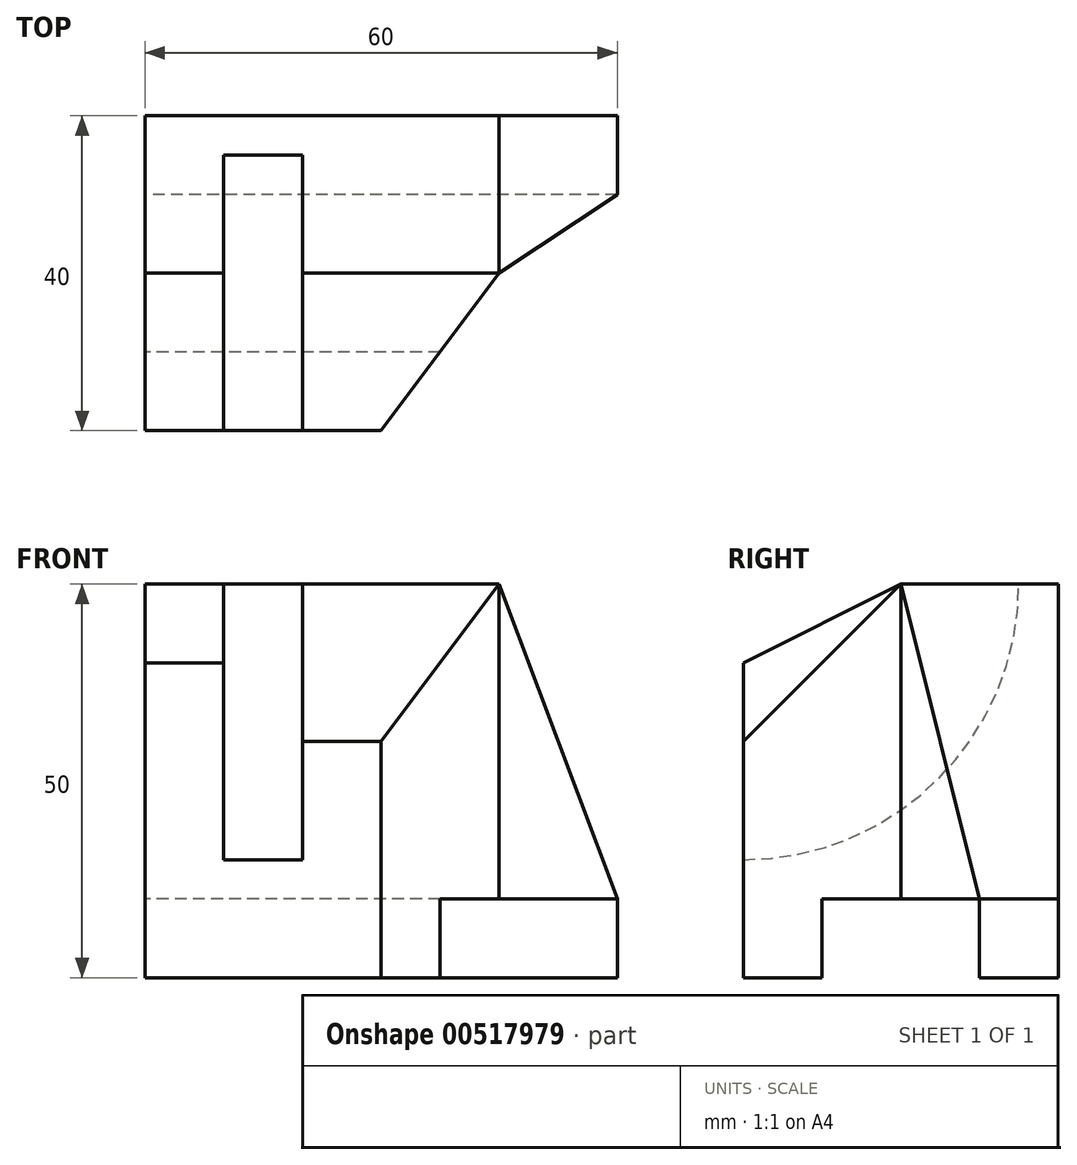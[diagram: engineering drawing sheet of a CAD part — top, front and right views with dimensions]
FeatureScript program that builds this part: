
annotation { "Feature Type Name" : "Feature", "Feature Type Description" : "" }
export const myFeature = defineFeature(function(context is Context, id is Id, definition is map)
    precondition{}
    {
        {
            var Q0;
            Q0=qCreatedBy(makeId("Top.planeOp"),FACE);
            var sketch = newSketch(context, id + "F0", { "sketchPlane" : qUnion([Q0])});
            skLineSegment(sketch, "E0.bottom", {"start": v(0, 0) * mm, "end": v(60, 0) * mm});
            skLineSegment(sketch, "E0.top", {"start": v(0, 40) * mm, "end": v(60, 40) * mm});
            skLineSegment(sketch, "E0.left", {"start": v(0, 0) * mm, "end": v(0, 40) * mm});
            skLineSegment(sketch, "E0.right", {"start": v(60, 0) * mm, "end": v(60, 40) * mm});
            skSolve(sketch);
        }
        {
            var Q0;
            Q0 = qSketchRegion(id + "F0", true);
            extrude(context, id + "F1", {"entities" : qUnion([Q0]), "depth" : 50 * mm, "offsetDistance" : 25 * mm});
        }
        {
            var Q0;
            Q0=makeQuery(id+"F1.opExtrude","CAP_FACE",FACE,{"disambiguationData":[OSD([sQuery(id+"F0.wireOp",EDGE,"E0.bottom"),sQuery(id+"F0.wireOp",EDGE,"E0.top"),sQuery(id+"F0.wireOp",EDGE,"E0.left"),sQuery(id+"F0.wireOp",EDGE,"E0.right")])],"isStart":true});
            var sketch = newSketch(context, id + "F2", { "sketchPlane" : qUnion([Q0])});
            skLineSegment(sketch, "E1.bottom", {"start": v(60, -10) * mm, "end": v(0, -10) * mm});
            skLineSegment(sketch, "E1.top", {"start": v(60, -30) * mm, "end": v(0, -30) * mm});
            skLineSegment(sketch, "E1.left", {"start": v(60, -10) * mm, "end": v(60, -30) * mm});
            skLineSegment(sketch, "E1.right", {"start": v(0, -10) * mm, "end": v(0, -30) * mm});
            skSolve(sketch);
        }
        {
            var Q0;
            Q0=makeQuery(id+"F2.imprint","IMPRINT",FACE,{"disambiguationData":[TD([[makeQuery(id+"F2.imprint","IMPRINT",EDGE,{"derivedFrom":sQuery(id+"F2.wireOp",EDGE,"E1.bottom")}),1.0]])]});
            extrude(context, id + "F3", {"entities" : qUnion([Q0]), "operationType" : NewBodyOperationType.REMOVE, "oppositeDirection" : true, "depth" : 10 * mm, "offsetDistance" : 25 * mm});
        }
        {
            var Q0;
            Q0=makeQuery(id+"F1.opExtrude","CAP_FACE",FACE,{"disambiguationData":[OSD([sQuery(id+"F0.wireOp",EDGE,"E0.bottom"),sQuery(id+"F0.wireOp",EDGE,"E0.top"),sQuery(id+"F0.wireOp",EDGE,"E0.left"),sQuery(id+"F0.wireOp",EDGE,"E0.right")])],"isStart":false});
            var sketch = newSketch(context, id + "F4", { "sketchPlane" : qUnion([Q0])});
            skLineSegment(sketch, "E2.bottom", {"start": v(10, 0) * mm, "end": v(20, 0) * mm});
            skLineSegment(sketch, "E2.top", {"start": v(10, 35) * mm, "end": v(20, 35) * mm});
            skLineSegment(sketch, "E2.left", {"start": v(10, 0) * mm, "end": v(10, 35) * mm});
            skLineSegment(sketch, "E2.right", {"start": v(20, 0) * mm, "end": v(20, 35) * mm});
            skSolve(sketch);
        }
        {
            var Q0;
            Q0=makeQuery(id+"F4.imprint","IMPRINT",FACE,{"disambiguationData":[TD([[makeQuery(id+"F4.imprint","IMPRINT",EDGE,{"derivedFrom":sQuery(id+"F4.wireOp",EDGE,"E2.bottom")}),1.0]])]});
            extrude(context, id + "F5", {"entities" : qUnion([Q0]), "operationType" : NewBodyOperationType.REMOVE, "oppositeDirection" : true, "depth" : 35 * mm, "offsetDistance" : 25 * mm});
        }
        {
            var Q0;
            Q0=makeQuery(id+"F5.boolean.opBoolean","COPY",EDGE,{"derivedFrom":makeQuery(id+"F5.opExtrude","CAP_EDGE",EDGE,{"disambiguationData":[OSD([sQuery(id+"F4.wireOp",EDGE,"E2.top")])],"isStart":false})});
            fillet(context, id + "F6", {"entities" : qUnion([Q0]), "radius" : 35 * mm, "tangentPropagation" : true, "allowEdgeOverflow" : false});
        }
        {
            var Q0;
            Q0=makeQuery(id+"F1.opExtrude","SWEPT_FACE",FACE,{"disambiguationData":[OSD([sQuery(id+"F0.wireOp",EDGE,"E0.left")])]});
            var sketch = newSketch(context, id + "F7", { "sketchPlane" : qUnion([Q0])});
            skLineSegment(sketch, "E3", {"start": v(-20, 50) * mm, "end": v(0, 40) * mm});
            skSolve(sketch);
        }
        {
            var Q0;
            {var subQ0=sQuery(id+"F7.wireOp",EDGE,"E3");Q0=makeQuery(id+"F7.imprint","IMPRINT",FACE,{"disambiguationData":[TD([[makeQuery(id+"F7.imprint","IMPRINT",EDGE,{"derivedFrom":subQ0}),1.0]])]});}
            extrude(context, id + "F8", {"entities" : qUnion([Q0]), "operationType" : NewBodyOperationType.REMOVE, "endBound" : BoundingType.UP_TO_NEXT, "oppositeDirection" : true, "depth" : 25 * mm, "offsetDistance" : 25 * mm});
        }
        {
            var Q0;
            Q0=makeQuery(id+"F1.opExtrude","CAP_FACE",FACE,{"disambiguationData":[OSD([sQuery(id+"F0.wireOp",EDGE,"E0.bottom"),sQuery(id+"F0.wireOp",EDGE,"E0.top"),sQuery(id+"F0.wireOp",EDGE,"E0.left"),sQuery(id+"F0.wireOp",EDGE,"E0.right")])],"isStart":false});
            var sketch = newSketch(context, id + "F9", { "sketchPlane" : qUnion([Q0])});
            skLineSegment(sketch, "E4", {"start": v(30, 0) * mm, "end": v(45, 20) * mm});
            skLineSegment(sketch, "E5", {"start": v(45, 20) * mm, "end": v(60, 20) * mm});
            skPoint(sketch, "E5.endSnap0", {"position": v(60, 20) * mm});
            skSolve(sketch);
        }
        {
            var Q0;
            {var subQ0=sQuery(id+"F9.wireOp",EDGE,"E4");Q0=makeQuery(id+"F9.imprint","IMPRINT",FACE,{"disambiguationData":[TD([[makeQuery(id+"F9.imprint","IMPRINT",EDGE,{"derivedFrom":subQ0}),-1.0]])]});}
            extrude(context, id + "F10", {"entities" : qUnion([Q0]), "operationType" : NewBodyOperationType.REMOVE, "endBound" : BoundingType.THROUGH_ALL, "oppositeDirection" : true, "depth" : 25 * mm, "offsetDistance" : 25 * mm});
        }
        {
            var Q0;
            Q0=makeQuery(id+"F1.opExtrude","CAP_FACE",FACE,{"disambiguationData":[OSD([sQuery(id+"F0.wireOp",EDGE,"E0.bottom"),sQuery(id+"F0.wireOp",EDGE,"E0.top"),sQuery(id+"F0.wireOp",EDGE,"E0.left"),sQuery(id+"F0.wireOp",EDGE,"E0.right")])],"isStart":false});
            var sketch = newSketch(context, id + "F11", { "sketchPlane" : qUnion([Q0])});
            skLineSegment(sketch, "E6", {"start": v(20, 20) * mm, "end": v(45, 20) * mm});
            skPoint(sketch, "E6.startSnap0", {"position": v(5, 20) * mm});
            skSolve(sketch);
        }
        {
            var Q0;
            Q0=makeQuery(id+"F10.boolean.opBoolean","COPY",FACE,{"derivedFrom":makeQuery(id+"F10.opExtrude","SWEPT_FACE",FACE,{"disambiguationData":[OSD([sQuery(id+"F9.wireOp",EDGE,"E4")])]})});
            var sketch = newSketch(context, id + "F12", { "sketchPlane" : qUnion([Q0])});
            skLineSegment(sketch, "E7", {"start": v(43, 50) * mm, "end": v(18, 30) * mm});
            skSolve(sketch);
        }
        {
            var Q0;
            {var subQ0=sQuery(id+"F11.wireOp",EDGE,"E6");Q0=makeQuery(id+"F11.imprint","IMPRINT",FACE,{"disambiguationData":[TD([[makeQuery(id+"F11.imprint","IMPRINT",EDGE,{"derivedFrom":subQ0}),-1.0]])]});}
            var Q1;
            Q1=sQuery(id+"F12.wireOp",EDGE,"E7");
            sweep(context, id + "F13", {"operationType" : NewBodyOperationType.REMOVE, "profiles" : qUnion([Q0]), "path" : qUnion([Q1])});
        }
        {
            var Q0;
            Q0=makeQuery(id+"F1.opExtrude","SWEPT_FACE",FACE,{"disambiguationData":[OSD([sQuery(id+"F0.wireOp",EDGE,"E0.bottom")])]});
            var sketch = newSketch(context, id + "F14", { "sketchPlane" : qUnion([Q0])});
            skLineSegment(sketch, "E8", {"start": v(10, 36.67) * mm, "end": v(10, 30) * mm});
            skLineSegment(sketch, "E9", {"start": v(10, 30) * mm, "end": v(5, 30) * mm});
            skLineSegment(sketch, "E10", {"start": v(5, 30) * mm, "end": v(10, 36.67) * mm});
            skSolve(sketch);
        }
        {
            var Q0;
            Q0=makeQuery(id+"F14.imprint","IMPRINT",FACE,{"disambiguationData":[TD([[makeQuery(id+"F14.imprint","IMPRINT",EDGE,{"derivedFrom":sQuery(id+"F14.wireOp",EDGE,"E8")}),-1.0]])]});
            var Q1;
            Q1=makeQuery(id+"F13.boolean.opBoolean","INTERSECT",EDGE,{"derivedFrom":[makeQuery(id+"F5.boolean.opBoolean","COPY",FACE,{"derivedFrom":makeQuery(id+"F5.opExtrude","SWEPT_FACE",FACE,{"disambiguationData":[OSD([sQuery(id+"F4.wireOp",EDGE,"E2.left")])]})}),makeQuery(id+"F13.opSweep","SWEPT_FACE",FACE,{"disambiguationData":[OSD([sQuery(id+"F11.wireOp",EDGE,"E6"),sQuery(id+"F12.wireOp",EDGE,"E7")])]})]});
            sweep(context, id + "F15", {"operationType" : NewBodyOperationType.ADD, "profiles" : qUnion([Q0]), "path" : qUnion([Q1])});
        }
        {
            var Q0;
            Q0=makeQuery(id+"F1.opExtrude","CAP_FACE",FACE,{"disambiguationData":[OSD([sQuery(id+"F0.wireOp",EDGE,"E0.bottom"),sQuery(id+"F0.wireOp",EDGE,"E0.top"),sQuery(id+"F0.wireOp",EDGE,"E0.left"),sQuery(id+"F0.wireOp",EDGE,"E0.right")])],"isStart":false});
            var sketch = newSketch(context, id + "F16", { "sketchPlane" : qUnion([Q0])});
            skLineSegment(sketch, "E11.bottom", {"start": v(60, 20) * mm, "end": v(45, 20) * mm});
            skLineSegment(sketch, "E11.top", {"start": v(60, 40) * mm, "end": v(45, 40) * mm});
            skLineSegment(sketch, "E11.left", {"start": v(60, 20) * mm, "end": v(60, 40) * mm});
            skLineSegment(sketch, "E11.right", {"start": v(45, 20) * mm, "end": v(45, 40) * mm});
            skSolve(sketch);
        }
        {
            var Q0;
            Q0=makeQuery(id+"F1.opExtrude","SWEPT_FACE",FACE,{"disambiguationData":[OSD([sQuery(id+"F0.wireOp",EDGE,"E0.top")])]});
            var sketch = newSketch(context, id + "F17", { "sketchPlane" : qUnion([Q0])});
            skLineSegment(sketch, "E12", {"start": v(-45, 50) * mm, "end": v(-60, 10) * mm});
            skSolve(sketch);
        }
        {
            var Q0;
            Q0=makeQuery(id+"F16.imprint","IMPRINT",FACE,{"disambiguationData":[TD([[makeQuery(id+"F16.imprint","IMPRINT",EDGE,{"derivedFrom":sQuery(id+"F16.wireOp",EDGE,"E11.bottom")}),1.0]])]});
            var Q1;
            Q1=sQuery(id+"F17.wireOp",EDGE,"E12");
            sweep(context, id + "F18", {"operationType" : NewBodyOperationType.REMOVE, "profiles" : qUnion([Q0]), "path" : qUnion([Q1])});
        }
        {
            var Q0;
            Q0=makeQuery(id+"F18.boolean.opBoolean","COPY",FACE,{"derivedFrom":makeQuery(id+"F18.opSweep","SWEPT_FACE",FACE,{"disambiguationData":[OSD([sQuery(id+"F16.wireOp",EDGE,"E11.right"),sQuery(id+"F17.wireOp",EDGE,"E12")])]})});
            var sketch = newSketch(context, id + "F19", { "sketchPlane" : qUnion([Q0])});
            skLineSegment(sketch, "E13", {"start": v(30, -11.7) * mm, "end": v(20, 31.02) * mm});
            skSolve(sketch);
        }
        {
            var Q0;
            Q0=makeQuery(id+"F19.imprint","IMPRINT",FACE,{"disambiguationData":[TD([[makeQuery(id+"F19.imprint","IMPRINT",EDGE,{"derivedFrom":sQuery(id+"F19.wireOp",EDGE,"E13")}),1.0]])]});
            var Q1;
            Q1=makeQuery(id+"F10.boolean.opBoolean","COPY",EDGE,{"derivedFrom":makeQuery(id+"F10.opExtrude","SWEPT_EDGE",EDGE,{"disambiguationData":[OSD([sQuery(id+"F9.wireOp",EDGE,"E4"),sQuery(id+"F9.wireOp",EDGE,"E5")])]})});
            sweep(context, id + "F20", {"operationType" : NewBodyOperationType.REMOVE, "profiles" : qUnion([Q0]), "path" : qUnion([Q1])});
        }
    });
